# Revit family: Bath-Alcove-KOHLER-Underscore-K-20201_
name_source: partatom
category: Plumbing Fixtures
units: mm (PartAtom-declared; Revit-internal decimal feet)

## family parameters
Cut with Voids When Loaded = No
Host = Face
Maintain Annotation Orientation = No
OmniClass Number = 23.31.15.00
OmniClass Title = Bathtubs
Part Type = Normal
Room Calculation Point = No
Round Connector Dimension = Use Diameter
Shared = No

## types (4) — shared parameters
ADA Compliant = Yes
Assembly Code = D2010500
CW Connection = No
Cold Water Inlet = Cold Water Inlet
Date Modified = 04/07/2022
Default Elevation = 0"
Drain Included = No
Finish = Kohler-Acrylic-0-White
HW Connection = No
Height = 20 1/4"
Hot Water Inlet = Hot Water Inlet
Length = 30"
Manufacturer = Kohler Co.
Master Format 2014 = 22 41 19
Master Format 2014 Name = Residential Bathtubs
Material = Acrylic
Product Documentation Link = https://www.us.kohler.com
Product Name = Underscore
Product Page URL = http://www.us.kohler.com
URL = https://www.us.kohler.com
Vent Connection = No
Waste Connection = Yes
Waste Water Outlet = Waste Water Outlet
WaterSense Certified = No
Width = 60"

## per-type parameters (varying)
| type | Description | Drain location | LA | LA_Symbolic | Model | RA | RA_Symbolic | RL | RR | Type |
| Slotted Left Drain, 0-White | 60inch x 30inch alcove bath with integral apron, integral flange, and left-hand drain | 9" | Yes | Yes | K-20201-LA-0 | No | No | No | No | 1 |
| Slotted Right Drain, 0-White | 60inch x 30inch alcove bath with integral apron, integral flange, and right-hand drain | 51" | No | No | K-20201-RA-0 | Yes | Yes | No | No | 2 |
| Round Left Drain, 0-White | 60inch x 30inch alcove bath with integral apron, left drain | 9" | Yes | No | K-20201-RL-0 | No | No | Yes | No | 3 |
| Round Right Drain, 0-White | 60inch x 30inch alcove bath with right drain | 51" | No | No | K-20201-RR-0 | Yes | No | No | Yes | 4 |

## geometry (parser evidence)
native form markers: Sweep x4
no freeform markers — native parametric forms only
